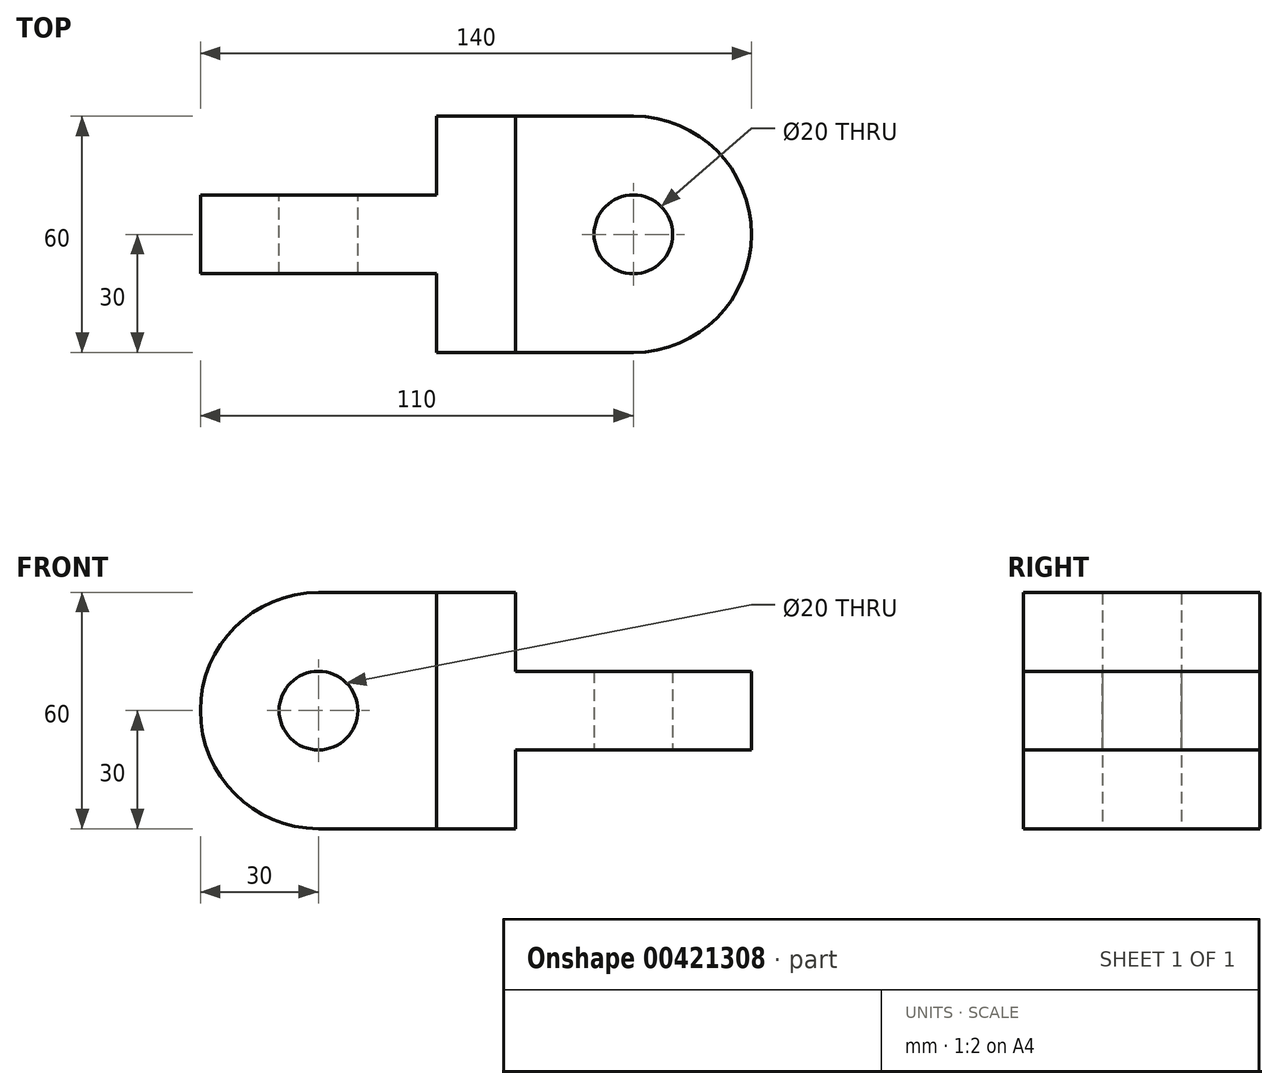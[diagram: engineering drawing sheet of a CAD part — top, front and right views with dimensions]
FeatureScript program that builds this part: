
annotation { "Feature Type Name" : "Feature", "Feature Type Description" : "" }
export const myFeature = defineFeature(function(context is Context, id is Id, definition is map)
    precondition{}
    {
        {
            var Q0;
            Q0=qCreatedBy(makeId("Front.planeOp"),FACE);
            var sketch = newSketch(context, id + "F0", { "sketchPlane" : qUnion([Q0])});
            skLineSegment(sketch, "E0.bottom", {"start": v(0, 30) * mm, "end": v(20, 30) * mm});
            skLineSegment(sketch, "E0.top", {"start": v(0, -30) * mm, "end": v(20, -30) * mm});
            skLineSegment(sketch, "E0.left", {"start": v(0, 30) * mm, "end": v(0, -30) * mm});
            skLineSegment(sketch, "E0.right", {"start": v(20, 30) * mm, "end": v(20, -30) * mm});
            skLineSegment(sketch, "E1.bottom", {"start": v(0, 30) * mm, "end": v(-30, 30) * mm});
            skLineSegment(sketch, "E1.top", {"start": v(0, -30) * mm, "end": v(-30, -30) * mm});
            skArc(sketch, "E2", {"start": v(-30, 30) * mm, "mid": v(-60, 0) * mm, "end": v(-30, -30) * mm});
            skCircle(sketch, "E3", {"center": v(-30, 0) * mm, "radius": 10 * mm});
            skSolve(sketch);
        }
        {
            var Q0;
            Q0=makeQuery(id+"F0.imprint","IMPRINT",FACE,{"disambiguationData":[TD([[makeQuery(id+"F0.imprint","IMPRINT",EDGE,{"derivedFrom":sQuery(id+"F0.wireOp",EDGE,"E0.bottom")}),-1.0]])]});
            extrude(context, id + "F1", {"entities" : qUnion([Q0]), "endBound" : BoundingType.SYMMETRIC, "depth" : 60 * mm});
        }
        {
            var Q0;
            Q0=makeQuery(id+"F0.imprint","IMPRINT",FACE,{"disambiguationData":[TD([[makeQuery(id+"F0.imprint","IMPRINT",EDGE,{"derivedFrom":sQuery(id+"F0.wireOp",EDGE,"E0.left")}),-1.0]])]});
            extrude(context, id + "F2", {"entities" : qUnion([Q0]), "operationType" : NewBodyOperationType.ADD, "endBound" : BoundingType.SYMMETRIC, "depth" : 20 * mm, "hasSecondDirection" : true, "secondDirectionOppositeDirection" : true, "secondDirectionDepth" : 25 * mm});
        }
        {
            var Q0;
            Q0=qCreatedBy(makeId("Top.planeOp"),FACE);
            var sketch = newSketch(context, id + "F3", { "sketchPlane" : qUnion([Q0])});
            skLineSegment(sketch, "E4.left", {"start": v(20, -30) * mm, "end": v(20, 30) * mm});
            skLineSegment(sketch, "E5.bottom", {"start": v(20, -30) * mm, "end": v(50, -30) * mm});
            skLineSegment(sketch, "E5.top", {"start": v(20, 30) * mm, "end": v(50, 30) * mm});
            skArc(sketch, "E6", {"start": v(50, -30) * mm, "mid": v(80, 0) * mm, "end": v(50, 30) * mm});
            skCircle(sketch, "E7", {"center": v(50, 0) * mm, "radius": 10 * mm});
            skSolve(sketch);
        }
        {
            var Q0;
            Q0=makeQuery(id+"F3.imprint","IMPRINT",FACE,{"disambiguationData":[TD([[makeQuery(id+"F3.imprint","IMPRINT",EDGE,{"derivedFrom":sQuery(id+"F3.wireOp",EDGE,"E4.left")}),-1.0]])]});
            extrude(context, id + "F4", {"entities" : qUnion([Q0]), "operationType" : NewBodyOperationType.ADD, "endBound" : BoundingType.SYMMETRIC, "depth" : 20 * mm});
        }
    });
